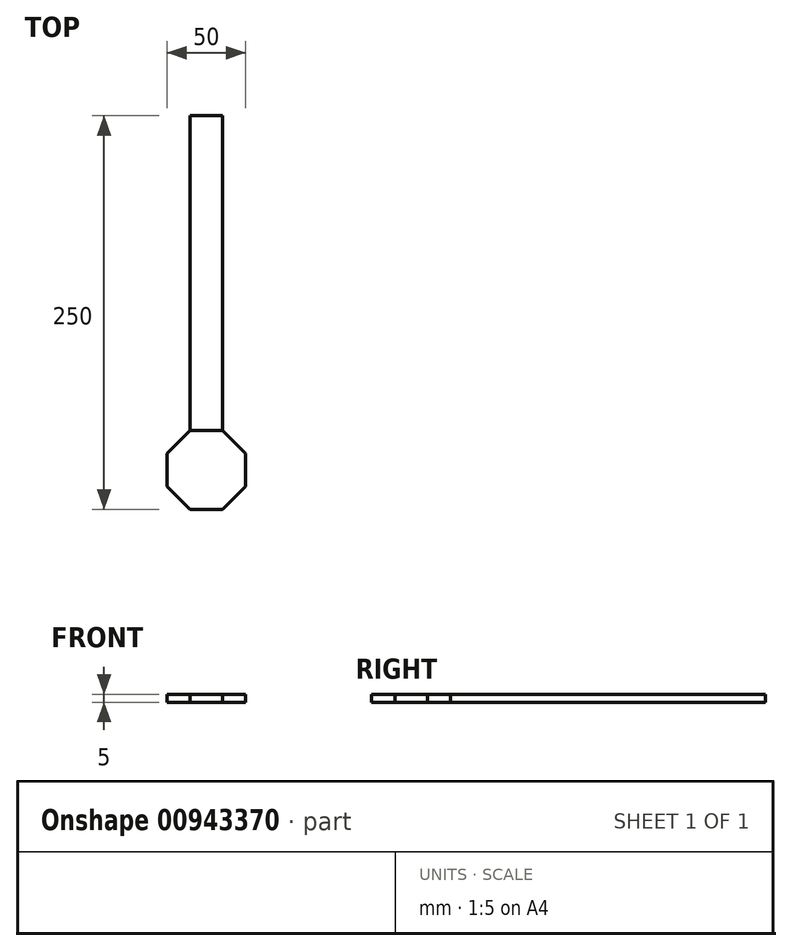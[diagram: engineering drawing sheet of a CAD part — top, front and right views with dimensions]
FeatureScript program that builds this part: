
annotation { "Feature Type Name" : "Feature", "Feature Type Description" : "" }
export const myFeature = defineFeature(function(context is Context, id is Id, definition is map)
    precondition{}
    {
        {
            var Q0;
            Q0=qCreatedBy(makeId("Top.planeOp"),FACE);
            var sketch = newSketch(context, id + "F0", { "sketchPlane" : qUnion([Q0])});
            skCircle(sketch, "E0.cCircle", {"center": v(0, 0) * mm, "radius": 25 * mm, "construction": true});
            skLineSegment(sketch, "E0.0", {"start": v(10.36, 25) * mm, "end": v(25, 10.36) * mm});
            skLineSegment(sketch, "E0.1", {"start": v(25, 10.36) * mm, "end": v(25, -10.36) * mm});
            skLineSegment(sketch, "E0.2", {"start": v(25, -10.36) * mm, "end": v(10.36, -25) * mm});
            skLineSegment(sketch, "E0.3", {"start": v(10.36, -25) * mm, "end": v(-10.36, -25) * mm});
            skLineSegment(sketch, "E0.4", {"start": v(-10.36, -25) * mm, "end": v(-25, -10.36) * mm});
            skLineSegment(sketch, "E0.5", {"start": v(-25, -10.36) * mm, "end": v(-25, 10.36) * mm});
            skLineSegment(sketch, "E0.6", {"start": v(-25, 10.36) * mm, "end": v(-10.36, 25) * mm});
            skLineSegment(sketch, "E0.7", {"start": v(-10.36, 25) * mm, "end": v(10.36, 25) * mm});
            skPoint(sketch, "E0.0.midPoint", {"position": v(17.68, 17.68) * mm});
            skSolve(sketch);
        }
        {
            var Q0;
            Q0 = qSketchRegion(id + "F0", true);
            extrude(context, id + "F1", {"entities" : qUnion([Q0]), "depth" : 5 * mm, "offsetDistance" : 25 * mm});
        }
        {
            var Q0;
            Q0=qCreatedBy(makeId("Top.planeOp"),FACE);
            var sketch = newSketch(context, id + "F2", { "sketchPlane" : qUnion([Q0])});
            skPoint(sketch, "E1", {"position": v(-10.36, 25) * mm});
            skPoint(sketch, "E2", {"position": v(10.36, 25) * mm});
            skLineSegment(sketch, "E3.bottom", {"start": v(-10.36, 25) * mm, "end": v(10.36, 25) * mm});
            skLineSegment(sketch, "E3.top", {"start": v(-10.36, 225) * mm, "end": v(10.36, 225) * mm});
            skLineSegment(sketch, "E3.left", {"start": v(-10.36, 25) * mm, "end": v(-10.36, 225) * mm});
            skLineSegment(sketch, "E3.right", {"start": v(10.36, 25) * mm, "end": v(10.36, 225) * mm});
            skSolve(sketch);
        }
        {
            var Q0;
            Q0 = qSketchRegion(id + "F2", true);
            extrude(context, id + "F3", {"entities" : qUnion([Q0]), "depth" : 5 * mm, "offsetDistance" : 25 * mm});
        }
    });
